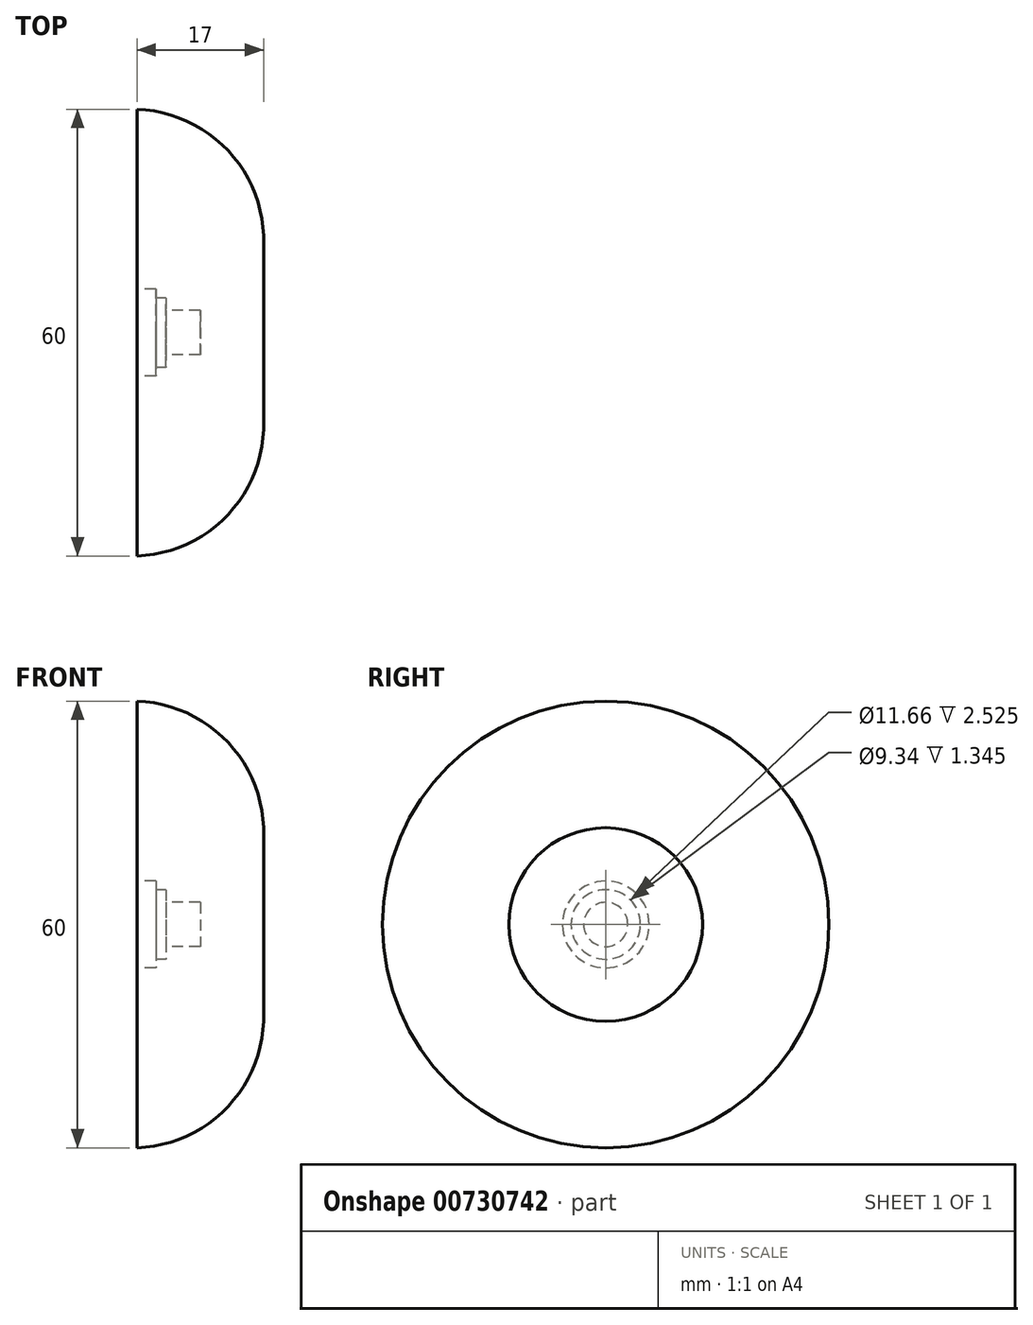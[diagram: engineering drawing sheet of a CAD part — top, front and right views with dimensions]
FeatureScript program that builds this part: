
annotation { "Feature Type Name" : "Feature", "Feature Type Description" : "" }
export const myFeature = defineFeature(function(context is Context, id is Id, definition is map)
    precondition{}
    {
        {
            var Q0;
            Q0=qCreatedBy(makeId("Front.planeOp"),FACE);
            var sketch = newSketch(context, id + "F0", { "sketchPlane" : qUnion([Q0])});
            skArc(sketch, "E0", {"start": v(0, 13) * mm, "mid": v(-5.16, 24.84) * mm, "end": v(-17, 30) * mm});
            skLineSegment(sketch, "E1", {"start": v(0, 13) * mm, "end": v(0, 0) * mm});
            skLineSegment(sketch, "E2", {"start": v(-8.5, 0) * mm, "end": v(-8.5, 2.97) * mm});
            skLineSegment(sketch, "E3", {"start": v(-8.5, 2.97) * mm, "end": v(-13.13, 2.97) * mm});
            skLineSegment(sketch, "E4", {"start": v(-13.13, 2.97) * mm, "end": v(-13.13, 4.67) * mm});
            skLineSegment(sketch, "E5", {"start": v(-13.13, 4.67) * mm, "end": v(-14.48, 4.67) * mm});
            skLineSegment(sketch, "E6", {"start": v(-14.48, 4.67) * mm, "end": v(-14.48, 5.83) * mm});
            skLineSegment(sketch, "E7", {"start": v(-14.48, 5.83) * mm, "end": v(-17, 5.83) * mm});
            skLineSegment(sketch, "E8", {"start": v(-17, 5.83) * mm, "end": v(-17, 30) * mm});
            skLineSegment(sketch, "E9", {"start": v(-8.5, 0) * mm, "end": v(0, 0) * mm});
            skSolve(sketch);
        }
        {
            var Q0;
            Q0=makeQuery(id+"F0.imprint","IMPRINT",FACE,{"disambiguationData":[TD([[makeQuery(id+"F0.imprint","IMPRINT",EDGE,{"derivedFrom":sQuery(id+"F0.wireOp",EDGE,"E0")}),1.0]])]});
            var Q1;
            Q1=sQuery(id+"F0.wireOp",EDGE,"E9");
            revolve(context, id + "F1", {"surfaceOperationType" : NewSurfaceOperationType.NEW, "entities" : qUnion([Q0]), "axis" : qUnion([Q1]), "revolveType" : RevolveType.FULL});
        }
    });
